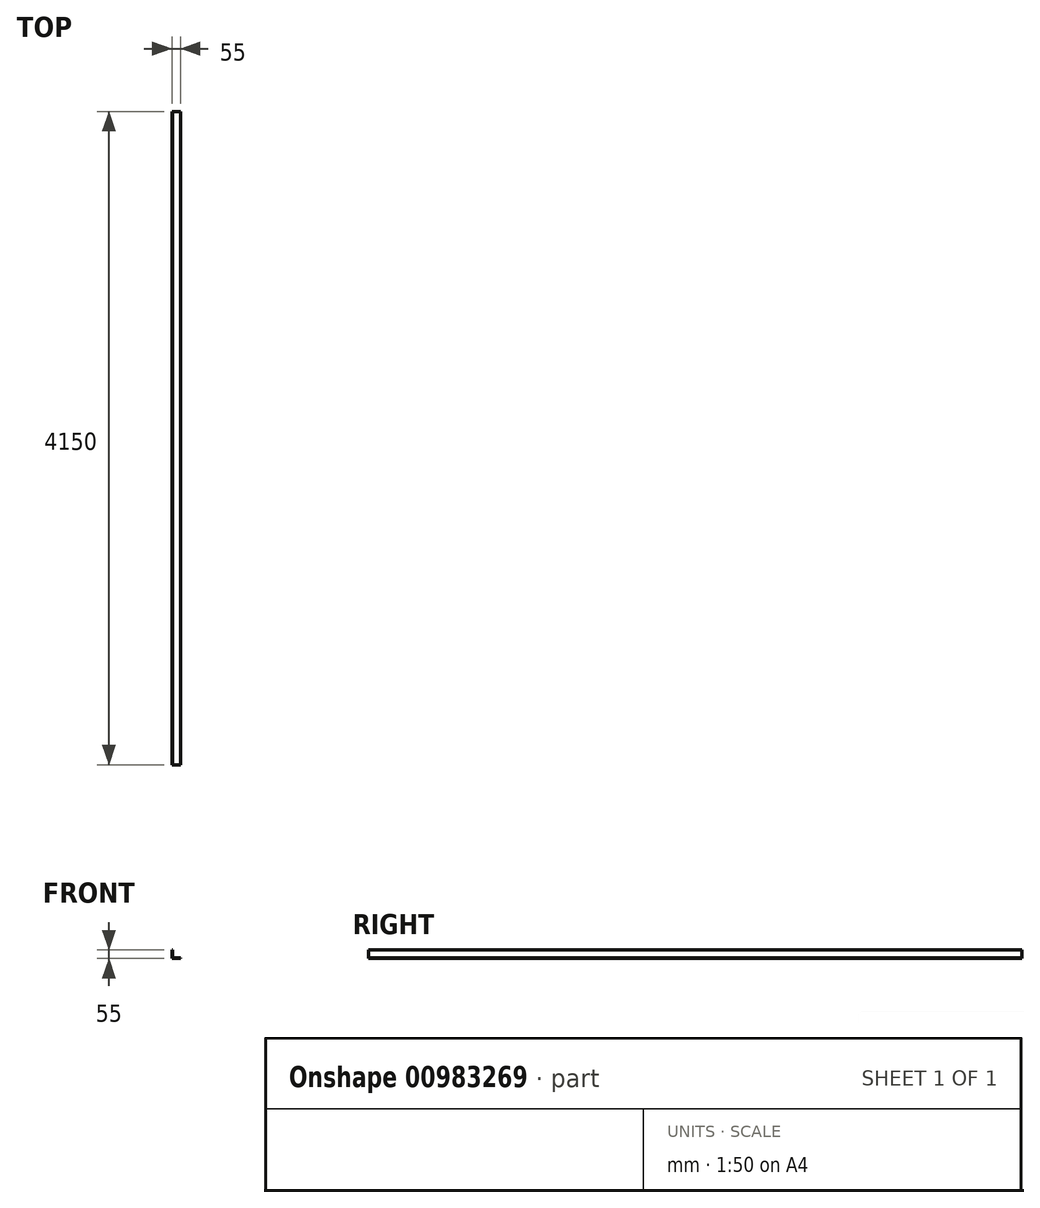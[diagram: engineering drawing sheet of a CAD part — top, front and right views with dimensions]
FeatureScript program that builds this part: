
annotation { "Feature Type Name" : "Feature", "Feature Type Description" : "" }
export const myFeature = defineFeature(function(context is Context, id is Id, definition is map)
    precondition{}
    {
        {
            var Q0;
            Q0=qCreatedBy(makeId("Front.planeOp"),FACE);
            var sketch = newSketch(context, id + "F0", { "sketchPlane" : qUnion([Q0])});
            skLineSegment(sketch, "E0", {"start": v(-124.36, 0) * mm, "end": v(-69.36, 0) * mm});
            skLineSegment(sketch, "E1", {"start": v(-69.36, 0) * mm, "end": v(-69.36, 5) * mm});
            skLineSegment(sketch, "E2", {"start": v(-69.36, 5) * mm, "end": v(-119.36, 5) * mm});
            skLineSegment(sketch, "E3", {"start": v(-119.36, 5) * mm, "end": v(-119.36, 55) * mm});
            skLineSegment(sketch, "E4", {"start": v(-119.36, 55) * mm, "end": v(-124.36, 55) * mm});
            skLineSegment(sketch, "E5", {"start": v(-124.36, 55) * mm, "end": v(-124.36, 0) * mm});
            skSolve(sketch);
        }
        {
            var Q0;
            Q0 = qSketchRegion(id + "F0", true);
            extrude(context, id + "F1", {"entities" : qUnion([Q0]), "depth" : 4150 * mm, "offsetDistance" : 25 * mm});
        }
    });
